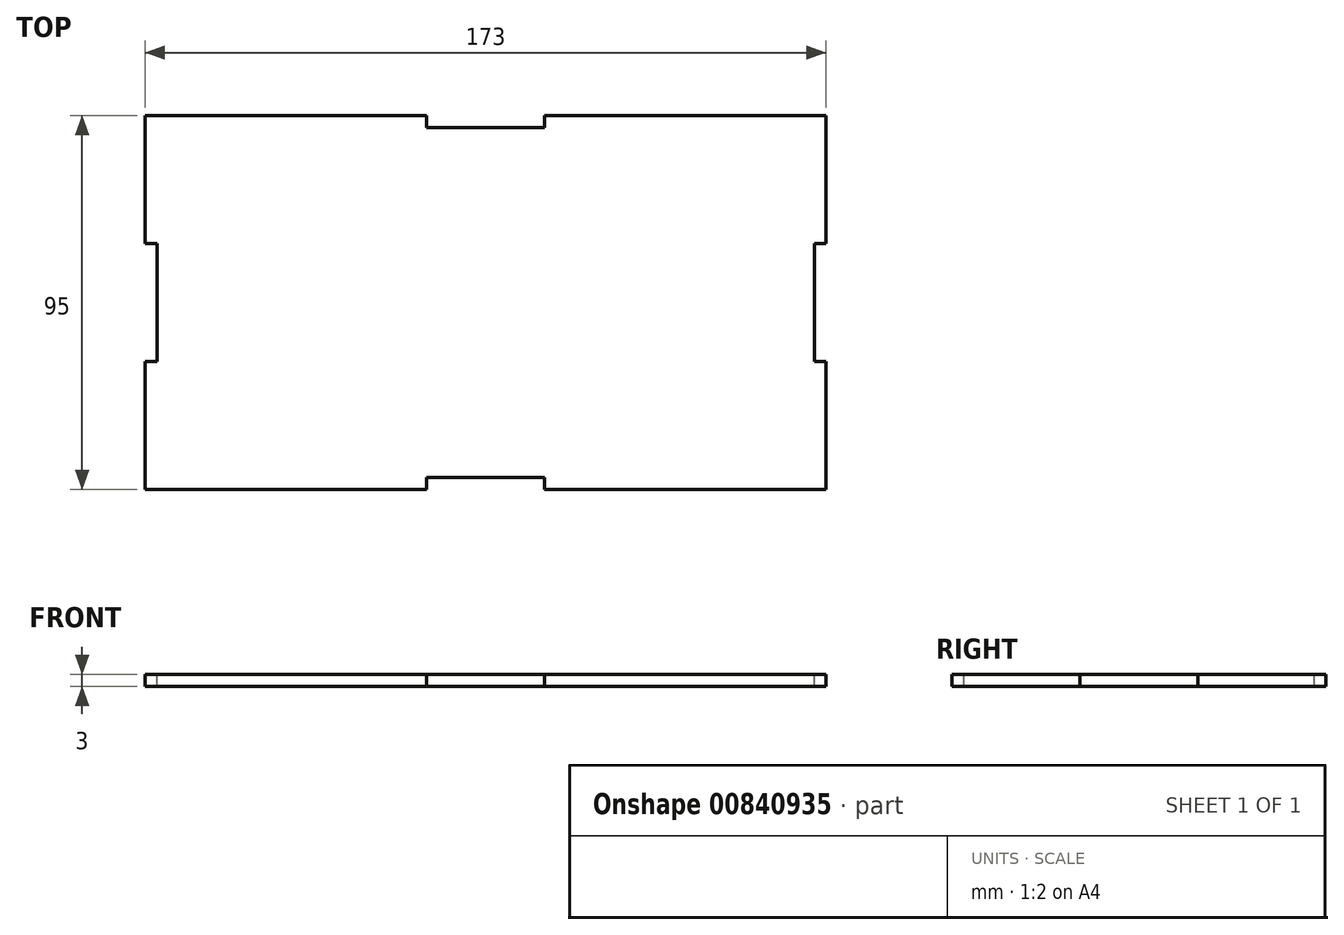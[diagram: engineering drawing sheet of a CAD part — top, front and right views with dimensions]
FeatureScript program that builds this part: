
annotation { "Feature Type Name" : "Feature", "Feature Type Description" : "" }
export const myFeature = defineFeature(function(context is Context, id is Id, definition is map)
    precondition{}
    {
        {
            var Q0;
            Q0=qCreatedBy(makeId("Top.planeOp"),FACE);
            var sketch = newSketch(context, id + "F0", { "sketchPlane" : qUnion([Q0])});
            skLineSegment(sketch, "E0.bottom", {"start": v(0, 0) * mm, "end": v(173, 0) * mm});
            skLineSegment(sketch, "E0.top", {"start": v(0, 95) * mm, "end": v(173, 95) * mm});
            skLineSegment(sketch, "E0.left", {"start": v(0, 0) * mm, "end": v(0, 95) * mm});
            skLineSegment(sketch, "E0.right", {"start": v(173, 0) * mm, "end": v(173, 95) * mm});
            skLineSegment(sketch, "E1", {"start": v(86.5, 95) * mm, "end": v(86.5, 0) * mm, "construction": true});
            skLineSegment(sketch, "E2", {"start": v(0, 47.5) * mm, "end": v(173, 47.5) * mm, "construction": true});
            skSolve(sketch);
        }
        {
            var Q0;
            Q0=makeQuery(id+"F0.imprint","IMPRINT",FACE,{"disambiguationData":[TD([[makeQuery(id+"F0.imprint","IMPRINT",EDGE,{"derivedFrom":sQuery(id+"F0.wireOp",EDGE,"E0.bottom")}),1.0]])]});
            extrude(context, id + "F1", {"entities" : qUnion([Q0]), "depth" : 3 * mm, "offsetDistance" : 25 * mm});
        }
        {
            var Q0;
            Q0=makeQuery(id+"F1.opExtrude","CAP_FACE",FACE,{"disambiguationData":[OSD([sQuery(id+"F0.wireOp",EDGE,"E0.bottom"),sQuery(id+"F0.wireOp",EDGE,"E0.top"),sQuery(id+"F0.wireOp",EDGE,"E0.left"),sQuery(id+"F0.wireOp",EDGE,"E0.right")])],"isStart":false});
            var sketch = newSketch(context, id + "F2", { "sketchPlane" : qUnion([Q0])});
            skLineSegment(sketch, "E3.bottom", {"start": v(71.5, 0) * mm, "end": v(101.5, 0) * mm});
            skLineSegment(sketch, "E3.top", {"start": v(71.5, 3) * mm, "end": v(101.5, 3) * mm});
            skLineSegment(sketch, "E3.left", {"start": v(71.5, 0) * mm, "end": v(71.5, 3) * mm});
            skLineSegment(sketch, "E3.right", {"start": v(101.5, 0) * mm, "end": v(101.5, 3) * mm});
            skLineSegment(sketch, "E4.MirrorCS", {"start": v(71.5, 95) * mm, "end": v(71.5, 92) * mm});
            skLineSegment(sketch, "E5.MirrorCS", {"start": v(101.5, 95) * mm, "end": v(101.5, 92) * mm});
            skLineSegment(sketch, "E6.MirrorCS", {"start": v(71.5, 92) * mm, "end": v(101.5, 92) * mm});
            skLineSegment(sketch, "E7.MirrorCS", {"start": v(71.5, 95) * mm, "end": v(101.5, 95) * mm});
            skLineSegment(sketch, "E8.bottom", {"start": v(0, 62.5) * mm, "end": v(3, 62.5) * mm});
            skLineSegment(sketch, "E8.top", {"start": v(0, 32.5) * mm, "end": v(3, 32.5) * mm});
            skLineSegment(sketch, "E8.left", {"start": v(0, 62.5) * mm, "end": v(0, 32.5) * mm});
            skLineSegment(sketch, "E8.right", {"start": v(3, 62.5) * mm, "end": v(3, 32.5) * mm});
            skLineSegment(sketch, "E9.MirrorCS", {"start": v(173, 32.5) * mm, "end": v(170, 32.5) * mm});
            skLineSegment(sketch, "E10.MirrorCS", {"start": v(173, 62.5) * mm, "end": v(170, 62.5) * mm});
            skLineSegment(sketch, "E11.MirrorCS", {"start": v(173, 62.5) * mm, "end": v(173, 32.5) * mm});
            skLineSegment(sketch, "E12.MirrorCS", {"start": v(170, 62.5) * mm, "end": v(170, 32.5) * mm});
            skSolve(sketch);
        }
        {
            var Q0;
            Q0 = qSketchRegion(id + "F2", true);
            extrude(context, id + "F3", {"entities" : qUnion([Q0]), "operationType" : NewBodyOperationType.REMOVE, "oppositeDirection" : true, "depth" : 25 * mm, "offsetDistance" : 25 * mm});
        }
    });
